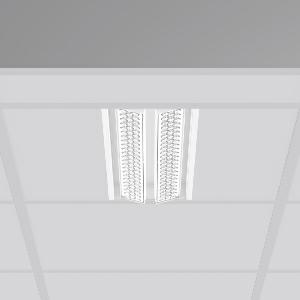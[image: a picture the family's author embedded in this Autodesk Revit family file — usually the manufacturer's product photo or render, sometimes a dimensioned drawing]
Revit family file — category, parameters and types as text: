
# Revit family: tx-move_901732_002_2_a7fe
name_source: partatom
category: Lighting Fixtures
units: mm (PartAtom-declared; Revit-internal decimal feet)

## family parameters
Cut with Voids When Loaded = No
Host = Face
Light Source = No
Part Type = Normal
Room Calculation Point = No
Round Connector Dimension = Use Diameter
Shared = No

## types (1)
- MultiLumen 1 (1 x LED Modul 927, 2000 lm, 2700)
    Apparent Load = 32 VA
    Approval mark = CE
    CIE Flux Codes = 90 97 99 100 100
    Color Rendering = 92
    Color Temperature = 2700
    Default Elevation = 1800 mm
    Description = Series: TX-MOVE
Einlege/Einbau-Flächenstrahler. Housing: sheet steel, powder-coated. 2xSwivel range: 90°. High-efficiency LED units with optimum light control thanks to clear plastic (PC) lens optics. Spezielle Mikrostrukturen reduzieren Gelbsaum. Symmetrical light distribution. Best colour rendering with CRI >90 for fresh products and coloured textiles. Suitable for laying in grid ceiling module 600. Connected converter included in separate gearbox.Suitable for through-wiring.MultiLumen: Luminous flux adjustable in 3 steps. Accessories: Mounting frame for installation in suspended ceilings. Environmentally friendly and resource-saving due to replaceable and recyclable components. 
Colour: traffic white, matt (RAL 9016)
Length: 597 mm
Width: 190 mm
Height: 39 mm
Cut-out length: 577.5 mm
Cut-out width: 174 mm
Recess height: 100 mm
Lamp: LED
Socket: without socket
Colour temperature: 2700K
Colour rendering index (CRI): 90
System power: 32 W
Rated luminous flux: 4000 lm
Luminous efficiency: 125 lm/W
System power 2: 43 W
Rated luminous flux 2: 5150 lm
Luminous efficiency 2: 120 lm/W
System power 3: 62 W
Rated luminous flux 3: 6750 lm
Luminous efficiency 3: 109 lm/W
Control gear: Regulated power supply
Protection class: I
Type of protection: IP 20
    Height = 0 mm  [stored 0 ft]
    Lamp = 1 x LED Modul 927
    Lamp Light Flux = 2000 lm
    Lamp count = 1
    Length = 597 mm
    Lifetime = 50000 h
    Luminous efficacy = 125 lm/W
    Manufacturer = RZB
    ModVariant = No
    Model = 901732.002.2
    Mounting Place = Ceiling, Wall
    Mounting Type = Recessed
    Number of Poles = 1
    OnlyDefault = Yes
    Power Factor = 1
    Product Name = TX-MOVE
    Product group = Recessed projectors
    ProductGroupID = 401
    Protection Class = Protection class I
    Protection Degree = IP 20
    RLX_Detail_Level = 1
    RLX_Emergency_Light_Flux = 0 lm
    RLX_Emergency_Type = 0
    RLX_Emergency_Type_DB = No
    RlxData = <blob elided: 35465 chars, md5=cbf20396>
    Socket = socket
    Standby Power = 0 W
    System Light Flux = 4000 lm
    System Power = 32 W
    Type Comments = MultiLumen 1
    Type Image = 901733.002.jpg
    URL = http://relux.com
    VarID = multilumen_1
    Voltage = 230 V
    Voltage Range = 220-240 V
    Weight = 0.00 kg
    Width = 190 mm  [stored 0.62336 ft]

note: [stored X ft] marks values corroborated as IEEE doubles in the binary element streams (Revit-internal decimal feet)

## geometry (parser evidence)
native form markers: Blend x4, Sweep x14
no freeform markers — native parametric forms only
